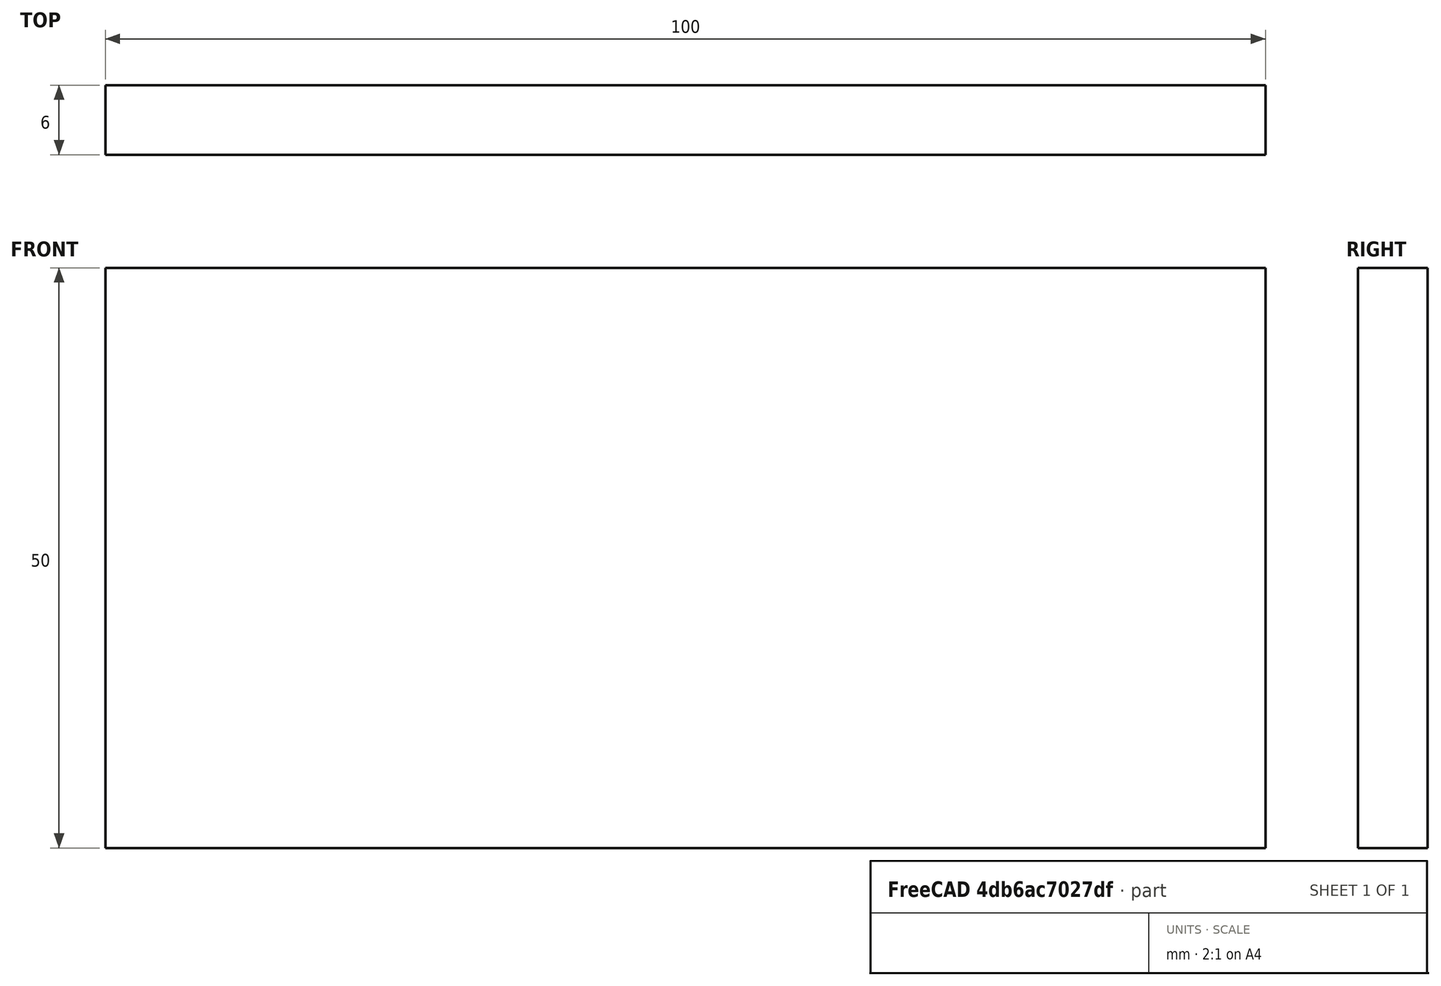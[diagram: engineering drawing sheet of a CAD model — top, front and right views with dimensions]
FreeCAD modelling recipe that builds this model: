
FCSTD DOCUMENT  (FreeCAD 0.15R4671 (Git))
Label: Flat Bar 100x6 EN10058 S235JR
License: All rights reserved
LicenseURL: http://en.wikipedia.org/wiki/All_rights_reserved
objects: Sketcher::SketchObject×1, Part::Extrusion×1
note: 2 computed .brp shape members not serialized (recipe doc carries the construction recipe); baked Part::Feature solids carry a one-line shape summary decoded from their .brp

FEATURE [Sketcher::SketchObject] Sketch
  sketch-geometry (4):
    g0: LineSegment StartX=-50 StartY=-3 StartZ=0 EndX=50 EndY=-3 EndZ=0
    g1: LineSegment StartX=50 StartY=-3 StartZ=0 EndX=50 EndY=3 EndZ=0
    g2: LineSegment StartX=50 StartY=3 StartZ=0 EndX=-50 EndY=3 EndZ=0
    g3: LineSegment StartX=-50 StartY=3 StartZ=0 EndX=-50 EndY=-3 EndZ=0
  constraints (12):
    c: Coincident(g0,g1)
    c: Coincident(g1,g2)
    c: Coincident(g2,g3)
    c: Coincident(g3,g0)
    c: Horizontal(g0)
    c: Horizontal(g2)
    c: Vertical(g1)
    c: Vertical(g3)
    c: Symmetric(g1,g2,g-2)
    c: Symmetric(g0,g1,g-1)
    c: DistanceY(g1) = 6
    c: DistanceX(g0) = 100
FEATURE [Part::Extrusion] Extrude  label="Flat Bar 100x6 EN10058 S235JR"
  Base = -> Sketch
  Dir = (0,0,50)
  Solid = true
